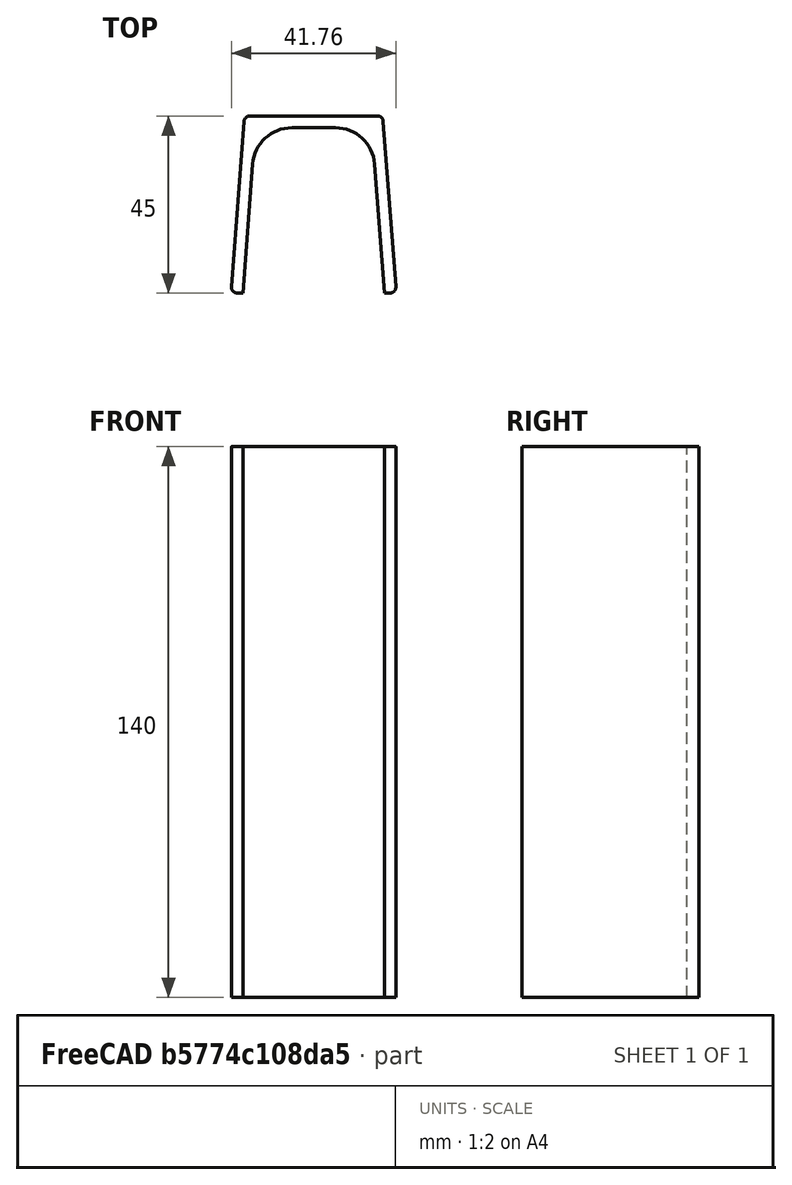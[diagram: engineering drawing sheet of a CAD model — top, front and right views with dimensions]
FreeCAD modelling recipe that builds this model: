
FCSTD DOCUMENT  (FreeCAD 2022.111R30764 (Git))
Label: sink protector
License: All rights reserved
LicenseURL: http://en.wikipedia.org/wiki/All_rights_reserved
objects: Sketcher::SketchObject×1, PartDesign::Pad×1, PartDesign::Body×1
note: 5 computed .brp shape members not serialized (recipe doc carries the construction recipe); baked Part::Feature solids carry a one-line shape summary decoded from their .brp

FEATURE [Sketcher::SketchObject] Sketch
  FullyConstrained = true
  MapMode = 5
  Support = -> [XY_Plane]
  TreeRank = 11
  sketch-geometry (18):
    g0: LineSegment StartX=16.1761 StartY=3 StartZ=0 EndX=-16.1761 EndY=3 EndZ=0
    g1: LineSegment StartX=-17.6718 StartY=1.61413 StartZ=0 EndX=-20.8768 EndY=-40.3859 EndZ=0
    g2: LineSegment StartX=-19.3812 StartY=-42 StartZ=0 EndX=-18 EndY=-42 EndZ=0
    g3: LineSegment StartX=-18 StartY=-42 StartZ=0 EndX=-15.5 EndY=-9.23911 EndZ=0
    g4: LineSegment StartX=-5.52899 StartY=0 StartZ=0 EndX=5.52899 EndY=0 EndZ=0
    g5: LineSegment StartX=15.5 StartY=-9.23911 StartZ=0 EndX=18 EndY=-42 EndZ=0
    g6: LineSegment StartX=18 StartY=-42 StartZ=0 EndX=19.3812 EndY=-42 EndZ=0
    g7: LineSegment StartX=20.8768 StartY=-40.3859 StartZ=0 EndX=17.6718 EndY=1.61413 EndZ=0
    g8: ArcOfCircle CenterX=-5.52899 CenterY=-10 CenterZ=0 NormalX=0 NormalY=0 NormalZ=1 AngleXU=0 Radius=10 StartAngle=1.5708 EndAngle=3.06543
    g9: GeomPoint [constr] X=-14.795 Y=0 Z=0
    g10: ArcOfCircle CenterX=5.52899 CenterY=-10 CenterZ=0 NormalX=0 NormalY=0 NormalZ=1 AngleXU=0 Radius=10 StartAngle=0.0761629 EndAngle=1.5708
    g11: GeomPoint [constr] X=14.795 Y=0 Z=0
    g12: ArcOfCircle CenterX=16.1761 CenterY=1.5 CenterZ=0 NormalX=0 NormalY=0 NormalZ=1 AngleXU=0 Radius=1.5 StartAngle=0.0761629 EndAngle=1.5708
    g13: ArcOfCircle CenterX=-16.1761 CenterY=1.5 CenterZ=0 NormalX=0 NormalY=0 NormalZ=1 AngleXU=0 Radius=1.5 StartAngle=1.5708 EndAngle=3.06543
    g14: ArcOfCircle CenterX=-19.3812 CenterY=-40.5 CenterZ=0 NormalX=0 NormalY=0 NormalZ=1 AngleXU=0 Radius=1.5 StartAngle=3.06543 EndAngle=4.71239
    g15: GeomPoint [constr] X=-21 Y=-42 Z=0
    g16: ArcOfCircle CenterX=19.3812 CenterY=-40.5 CenterZ=0 NormalX=0 NormalY=0 NormalZ=1 AngleXU=0 Radius=1.5 StartAngle=4.71239 EndAngle=6.35935
    g17: GeomPoint [constr] X=21 Y=-42 Z=0
  constraints (42):
    c: Horizontal(g2)
    c: Coincident(g2,g3)
    c: Horizontal(g4)
    c: Coincident(g5,g6)
    c: PointOnObject(g9,g4)
    c: PointOnObject(g9,g3)
    c: Tangent(g4,g8) = 1.5708
    c: Tangent(g3,g8) = 1.5708
    c: PointOnObject(g11,g4)
    c: PointOnObject(g11,g5)
    c: Tangent(g4,g10) = 1.5708
    c: Tangent(g5,g10) = 1.5708
    c: Equal(g8,g10)
    c: Diameter(g8) = 20
    c: DistanceX(g3,g5) = 31
    c: Symmetric(g2,g5,g-2)
    c: Horizontal(g6)
    c: DistanceX(g2,g5) = 36
    c: DistanceX(g15,g2) = 3
    c: PointOnObject(g4,g-1)
    c: Tangent(g0,g12) = -1.5708
    c: Tangent(g7,g12) = -1.5708
    c: Tangent(g0,g13) = -1.5708
    c: Tangent(g1,g13) = -1.5708
    c: Equal(g13,g12)
    c: Diameter(g13) = 3
    c: DistanceY(g2,g4) = 42
    c: Symmetric(g0,g0,g-2)
    c: Parallel(g1,g3)
    c: Parallel(g5,g7)
    c: DistanceY(g4,g0) = 3
    c: PointOnObject(g15,g1)
    c: PointOnObject(g15,g2)
    c: Tangent(g1,g14) = -1.5708
    c: Tangent(g2,g14) = -1.5708
    c: PointOnObject(g17,g7)
    c: PointOnObject(g17,g6)
    c: Tangent(g7,g16) = -1.5708
    c: Tangent(g6,g16) = -1.5708
    c: Equal(g14,g16)
    c: Diameter(g14) = 3
    c: Equal(g6,g2)
FEATURE [PartDesign::Pad] Pad
  AddSubType = 0
  AlongSketchNormal = false
  CheckUpToFaceLimits = true
  ClaimChildren = false
  Direction = (0,0,1)
  Fit = 0
  FitJoin = 0
  InnerFit = 0
  InnerFitJoin = 0
  InnerTaperAngle = 0
  InnerTaperAngleRev = 0
  Length = 140
  Length2 = 100
  Linearize = true
  NewSolid = false
  Profile = -> Sketch
  Suppress = false
  TreeRank = 12
  Type = 0
  _ProfileBasedVersion = 1
FEATURE [PartDesign::Body] Body
  AutoGroupSolids = false
  ExportMode = 0
  Group = -> [Sketch,Pad]
  Origin = -> Origin
  Tip = -> Pad
  TreeRank = 10
  _ExportChildren = -> [Pad]
  _GroupVersion = 1
